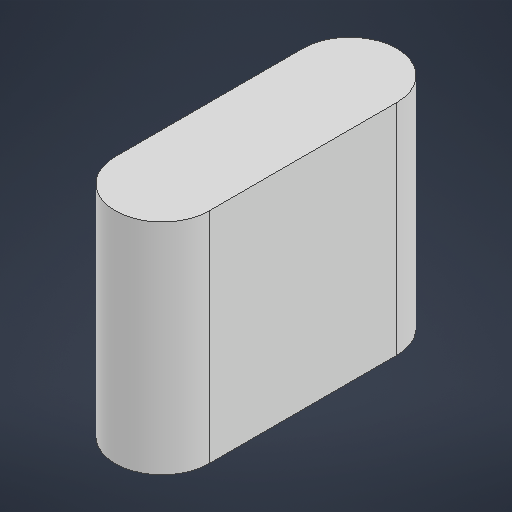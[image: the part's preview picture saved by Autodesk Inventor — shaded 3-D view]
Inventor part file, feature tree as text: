
AUTODESK INVENTOR PART (.ipt)
format: ipt  version: 2025.3 (Build 293356000, 356)  size: 177,152 bytes
history: native  units: mm
features: extrude x2, sketch x2, plane x1, projected_geometry x1
ambient origin geometry x8: Origin, YZ Plane, XZ Plane, XY Plane, X Axis, Y Axis, Z Axis, Center Point
bodies: Solid1 (feature_tree)
feature tree (6):
  extrude  "Extrusion1"  Depth=3.0mm
  plane  "Work Plane2"
  extrude  "Extrusion3"  Depth=3.0mm
  sketch  "Sketch1"  dims[d0=12.0mm d1=3.0mm]
  sketch  "Sketch3"  dims[d3=14.0mm d4=0.0mm d12=3.0mm d13=7.0mm d14=3.0mm d15=5.0mm d16=0.0mm d5=0.5mm d6=0.872665mm]
  projected_geometry  "Projected Loop1"
